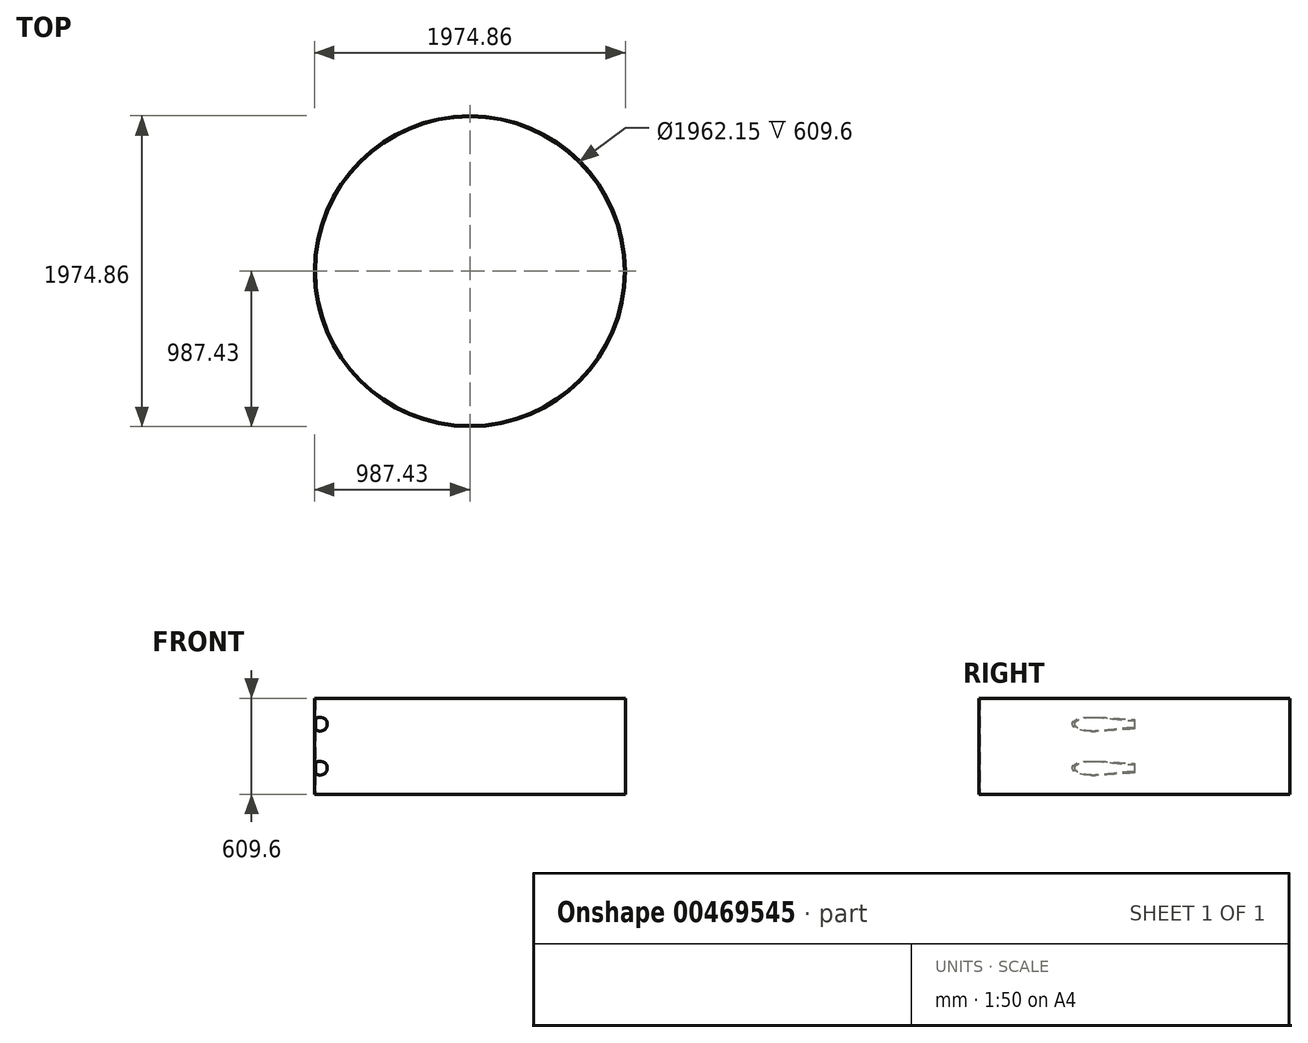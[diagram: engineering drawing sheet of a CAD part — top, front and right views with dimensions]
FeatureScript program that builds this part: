
annotation { "Feature Type Name" : "Feature", "Feature Type Description" : "" }
export const myFeature = defineFeature(function(context is Context, id is Id, definition is map)
    precondition{}
    {
        {
            var Q0;
            Q0=qCreatedBy(makeId("Top.planeOp"),FACE);
            var sketch = newSketch(context, id + "F0", { "sketchPlane" : qUnion([Q0])});
            skCircle(sketch, "E0", {"center": v(0, 0) * mm, "radius": 987.43 * mm});
            skCircle(sketch, "E1", {"center": v(0, 0) * mm, "radius": 981.08 * mm});
            skSolve(sketch);
        }
        {
            var Q0;
            Q0 = qSketchRegion(id + "F0", true);
            extrude(context, id + "F1", {"entities" : qUnion([Q0]), "depth" : 609.6 * mm, "offsetDistance" : 25.4 * mm});
        }
        {
            var Q0;
            Q0=qCreatedBy(makeId("Front.planeOp"),FACE);
            var sketch = newSketch(context, id + "F2", { "sketchPlane" : qUnion([Q0])});
            skCircle(sketch, "E2", {"center": v(-949.45, 444.5) * mm, "radius": 44.45 * mm});
            skCircle(sketch, "E3", {"center": v(-949.45, 165.1) * mm, "radius": 44.45 * mm});
            skSolve(sketch);
        }
        {
            var Q0;
            Q0 = qSketchRegion(id + "F2", true);
            extrude(context, id + "F3", {"entities" : qUnion([Q0]), "operationType" : NewBodyOperationType.REMOVE, "endBound" : BoundingType.THROUGH_ALL, "depth" : 25.4 * mm, "offsetDistance" : 25.4 * mm});
        }
    });
